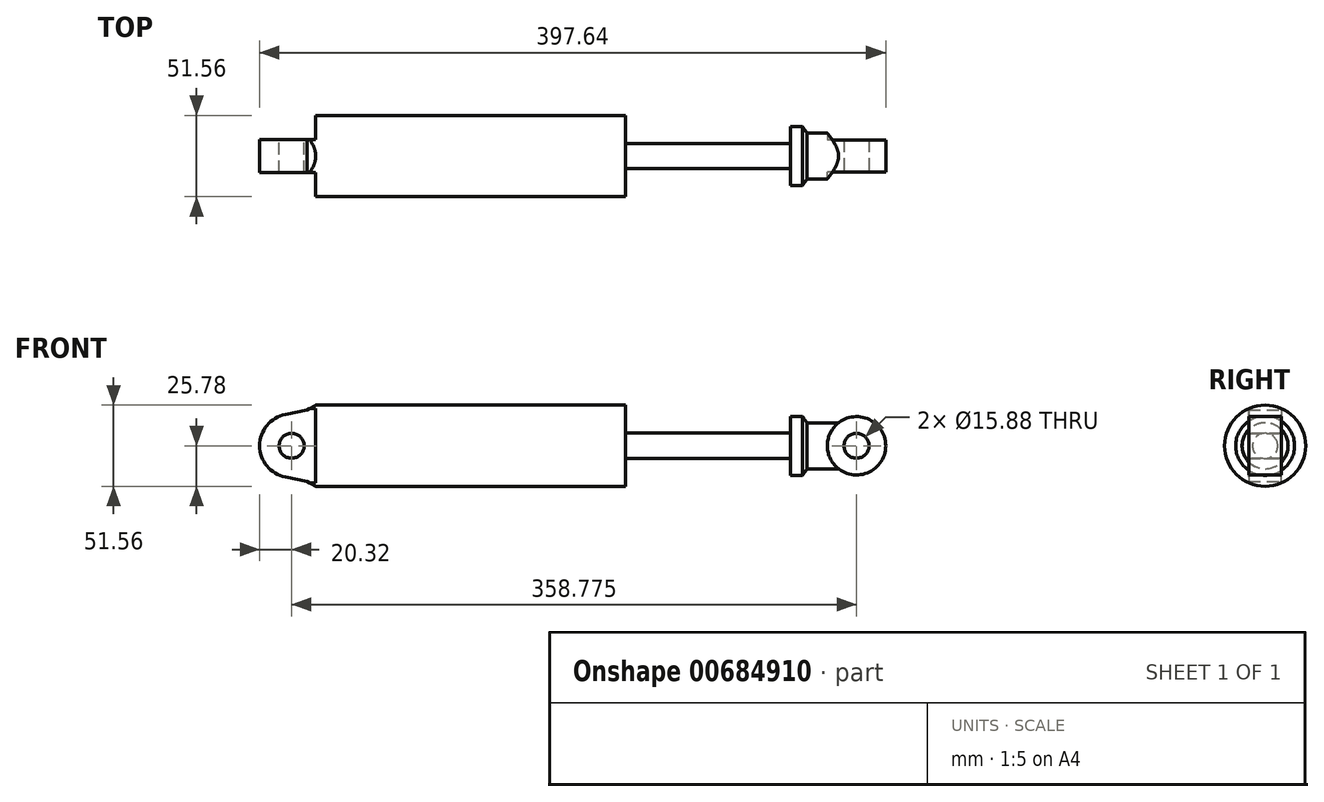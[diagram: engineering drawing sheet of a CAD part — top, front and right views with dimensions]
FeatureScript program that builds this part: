
annotation { "Feature Type Name" : "Feature", "Feature Type Description" : "" }
export const myFeature = defineFeature(function(context is Context, id is Id, definition is map)
    precondition{}
    {
        {
            var Q0;
            Q0=qCreatedBy(makeId("Front.planeOp"),FACE);
            var sketch = newSketch(context, id + "F0", { "sketchPlane" : qUnion([Q0])});
            skLineSegment(sketch, "E0", {"start": v(-164.73, 0) * mm, "end": v(453.96, 0) * mm, "construction": true});
            skLineSegment(sketch, "E1", {"start": v(0, 25.78) * mm, "end": v(232.41, 25.78) * mm});
            skLineSegment(sketch, "E2", {"start": v(232.41, 25.78) * mm, "end": v(232.41, 8) * mm});
            skLineSegment(sketch, "E3", {"start": v(232.41, 8) * mm, "end": v(337.19, 8) * mm});
            skLineSegment(sketch, "E4", {"start": v(337.19, 8) * mm, "end": v(337.19, 18.73) * mm});
            skLineSegment(sketch, "E5", {"start": v(337.19, 18.73) * mm, "end": v(344.8, 18.73) * mm});
            skLineSegment(sketch, "E6", {"start": v(344.8, 18.73) * mm, "end": v(347.6, 14.6) * mm});
            skLineSegment(sketch, "E7", {"start": v(347.6, 14.6) * mm, "end": v(409.83, 14.6) * mm});
            skLineSegment(sketch, "E8", {"start": v(0, 0) * mm, "end": v(409.83, 0) * mm});
            skLineSegment(sketch, "E9", {"start": v(409.83, 0) * mm, "end": v(409.83, 14.6) * mm});
            skLineSegment(sketch, "E10", {"start": v(0, 25.78) * mm, "end": v(0, 0) * mm});
            skSolve(sketch);
        }
        {
            var Q0;
            Q0 = qSketchRegion(id + "F0", true);
            var Q1;
            Q1=sQuery(id+"F0.wireOp",EDGE,"E0");
            revolve(context, id + "F1", {"surfaceOperationType" : NewSurfaceOperationType.NEW, "entities" : qUnion([Q0]), "axis" : qUnion([Q1]), "revolveType" : RevolveType.FULL});
        }
        {
            var Q0;
            Q0=makeQuery(id+"F1.opRevolve","SWEPT_FACE",FACE,{"disambiguationData":[OSD([sQuery(id+"F0.wireOp",EDGE,"E10")])]});
            var sketch = newSketch(context, id + "F2", { "sketchPlane" : qUnion([Q0])});
            skLineSegment(sketch, "E11", {"start": v(0, 48.27) * mm, "end": v(0, -54.75) * mm, "construction": true});
            skLineSegment(sketch, "E12", {"start": v(-46.95, 0) * mm, "end": v(40.07, 0) * mm, "construction": true});
            skLineSegment(sketch, "E13.bottom", {"start": v(48.51, 31.75) * mm, "end": v(10.41, 31.75) * mm});
            skLineSegment(sketch, "E13.top", {"start": v(48.51, -31.75) * mm, "end": v(10.41, -31.75) * mm});
            skLineSegment(sketch, "E13.left", {"start": v(48.51, 31.75) * mm, "end": v(48.51, -31.75) * mm});
            skLineSegment(sketch, "E13.right", {"start": v(10.41, 31.75) * mm, "end": v(10.41, -31.75) * mm});
            skPoint(sketch, "E13.middle", {"position": v(29.46, 0) * mm});
            skLineSegment(sketch, "E14.MirrorCS", {"start": v(-48.51, 31.75) * mm, "end": v(-48.51, -31.75) * mm});
            skLineSegment(sketch, "E15.MirrorCS", {"start": v(-48.51, 31.75) * mm, "end": v(-10.41, 31.75) * mm});
            skPoint(sketch, "E16.MirrorP", {"position": v(-29.46, 0) * mm});
            skLineSegment(sketch, "E17.MirrorCS", {"start": v(-48.51, -31.75) * mm, "end": v(-10.41, -31.75) * mm});
            skLineSegment(sketch, "E18.MirrorCS", {"start": v(-10.41, 31.75) * mm, "end": v(-10.41, -31.75) * mm});
            skSolve(sketch);
        }
        {
            var Q0;
            Q0 = qSketchRegion(id + "F2", true);
            extrude(context, id + "F3", {"entities" : qUnion([Q0]), "operationType" : NewBodyOperationType.REMOVE, "oppositeDirection" : true, "depth" : 35.56 * mm, "offsetDistance" : 25.4 * mm});
        }
        {
            var Q0;
            Q0=makeQuery(id+"F3.boolean.opBoolean","COPY",FACE,{"derivedFrom":makeQuery(id+"F3.opExtrude","SWEPT_FACE",FACE,{"disambiguationData":[OSD([sQuery(id+"F2.wireOp",EDGE,"E18.MirrorCS")])]})});
            var sketch = newSketch(context, id + "F4", { "sketchPlane" : qUnion([Q0])});
            skCircle(sketch, "E19", {"center": v(-20.32, 0) * mm, "radius": 20.32 * mm, "construction": true});
            skLineSegment(sketch, "E20", {"start": v(-35.56, 25.78) * mm, "end": v(-30.06, 22.6) * mm});
            skLineSegment(sketch, "E21", {"start": v(0, 0) * mm, "end": v(-64.15, 0) * mm, "construction": true});
            skLineSegment(sketch, "E22", {"start": v(-35.56, 25.78) * mm, "end": v(-35.56, -25.78) * mm, "construction": true});
            skLineSegment(sketch, "E23", {"start": v(-30.06, 22.6) * mm, "end": v(-16.43, 19.94) * mm});
            skLineSegment(sketch, "E24.MirrorCS", {"start": v(-30.06, -22.6) * mm, "end": v(-16.43, -19.94) * mm});
            skLineSegment(sketch, "E25.MirrorCS", {"start": v(-35.56, -25.78) * mm, "end": v(-30.06, -22.6) * mm});
            skArc(sketch, "E26", {"start": v(-16.43, 19.94) * mm, "mid": v(0, 0) * mm, "end": v(-16.43, -19.94) * mm});
            skCircle(sketch, "E27", {"center": v(-20.32, 0) * mm, "radius": 7.94 * mm});
            skLineSegment(sketch, "E28", {"start": v(-35.56, 25.78) * mm, "end": v(10.16, 25.78) * mm});
            skLineSegment(sketch, "E29.MirrorCS", {"start": v(-35.56, -25.78) * mm, "end": v(10.16, -25.78) * mm});
            skLineSegment(sketch, "E30", {"start": v(10.16, -25.78) * mm, "end": v(10.16, 25.78) * mm});
            skSolve(sketch);
        }
        {
            var Q0;
            Q0 = qSketchRegion(id + "F4", true);
            var Q1;
            Q1=makeQuery(id+"F3.boolean.opBoolean","COPY",FACE,{"derivedFrom":makeQuery(id+"F3.opExtrude","SWEPT_FACE",FACE,{"disambiguationData":[OSD([sQuery(id+"F2.wireOp",EDGE,"E13.right")])]})});
            extrude(context, id + "F5", {"entities" : qUnion([Q0]), "operationType" : NewBodyOperationType.REMOVE, "endBound" : BoundingType.UP_TO_SURFACE, "oppositeDirection" : true, "depth" : 25.4 * mm, "endBoundEntityFace" : qUnion([Q1]), "offsetDistance" : 25.4 * mm});
        }
        {
            var Q0;
            Q0=makeQuery(id+"F1.opRevolve","SWEPT_FACE",FACE,{"disambiguationData":[OSD([sQuery(id+"F0.wireOp",EDGE,"E9")])]});
            var sketch = newSketch(context, id + "F6", { "sketchPlane" : qUnion([Q0])});
            skLineSegment(sketch, "E31", {"start": v(-25.06, 0) * mm, "end": v(10.16, 0) * mm, "construction": true});
            skLineSegment(sketch, "E32", {"start": v(0, 36.45) * mm, "end": v(0, -31.45) * mm, "construction": true});
            skLineSegment(sketch, "E33.bottom", {"start": v(10.16, 12.7) * mm, "end": v(35.56, 12.7) * mm});
            skLineSegment(sketch, "E33.top", {"start": v(10.16, -12.7) * mm, "end": v(35.56, -12.7) * mm});
            skLineSegment(sketch, "E33.left", {"start": v(10.16, 12.7) * mm, "end": v(10.16, -12.7) * mm});
            skLineSegment(sketch, "E33.right", {"start": v(35.56, 12.7) * mm, "end": v(35.56, -12.7) * mm});
            skLineSegment(sketch, "E34.MirrorCS", {"start": v(-35.56, 12.7) * mm, "end": v(-35.56, -12.7) * mm});
            skLineSegment(sketch, "E35.MirrorCS", {"start": v(-10.16, 12.7) * mm, "end": v(-35.56, 12.7) * mm});
            skLineSegment(sketch, "E36.MirrorCS", {"start": v(-10.16, 12.7) * mm, "end": v(-10.16, -12.7) * mm});
            skLineSegment(sketch, "E37.MirrorCS", {"start": v(-10.16, -12.7) * mm, "end": v(-35.56, -12.7) * mm});
            skSolve(sketch);
        }
        {
            var Q0;
            Q0 = qSketchRegion(id + "F6", true);
            extrude(context, id + "F7", {"entities" : qUnion([Q0]), "operationType" : NewBodyOperationType.REMOVE, "oppositeDirection" : true, "depth" : 44.7 * mm, "offsetDistance" : 25.4 * mm});
        }
        {
            var Q0;
            Q0=makeQuery(id+"F7.boolean.opBoolean","COPY",FACE,{"derivedFrom":makeQuery(id+"F7.opExtrude","SWEPT_FACE",FACE,{"disambiguationData":[OSD([sQuery(id+"F6.wireOp",EDGE,"E33.left")])]})});
            var sketch = newSketch(context, id + "F8", { "sketchPlane" : qUnion([Q0])});
            skLineSegment(sketch, "E38", {"start": v(-418.1, 0) * mm, "end": v(-291.68, 0) * mm, "construction": true});
            skCircle(sketch, "E39", {"center": v(-20.32, 0) * mm, "radius": 7.74 * mm, "construction": true});
            skCircle(sketch, "E40", {"center": v(-379.1, 0) * mm, "radius": 18.54 * mm});
            skSolve(sketch);
        }
        {
            var Q0;
            Q0 = qSketchRegion(id + "F8", true);
            var Q1;
            Q1=makeQuery(id+"F7.boolean.opBoolean","COPY",FACE,{"derivedFrom":makeQuery(id+"F7.opExtrude","SWEPT_FACE",FACE,{"disambiguationData":[OSD([sQuery(id+"F6.wireOp",EDGE,"E36.MirrorCS")])]})});
            extrude(context, id + "F9", {"entities" : qUnion([Q0]), "operationType" : NewBodyOperationType.ADD, "endBound" : BoundingType.UP_TO_SURFACE, "oppositeDirection" : true, "depth" : 25.4 * mm, "endBoundEntityFace" : qUnion([Q1]), "offsetDistance" : 25.4 * mm});
        }
        {
            var Q0;
            Q0=qCreatedBy(makeId("Front.planeOp"),FACE);
            var sketch = newSketch(context, id + "F10", { "sketchPlane" : qUnion([Q0])});
            skLineSegment(sketch, "E41", {"start": v(-423.32, 0) * mm, "end": v(-348.96, 0) * mm, "construction": true});
            skLineSegment(sketch, "E42", {"start": v(418.77, 0) * mm, "end": v(354.73, 0) * mm, "construction": true});
            skCircle(sketch, "E43", {"center": v(379.1, 0) * mm, "radius": 6.7 * mm, "construction": true});
            skArc(sketch, "E44", {"start": v(390.52, 14.6) * mm, "mid": v(397.64, 0) * mm, "end": v(390.52, -14.6) * mm});
            skLineSegment(sketch, "E45", {"start": v(390.52, 14.6) * mm, "end": v(409.83, 14.6) * mm});
            skLineSegment(sketch, "E46", {"start": v(390.52, -14.6) * mm, "end": v(409.83, -14.6) * mm});
            skLineSegment(sketch, "E47", {"start": v(409.83, 14.6) * mm, "end": v(409.83, -14.6) * mm});
            skSolve(sketch);
        }
        {
            var Q0;
            Q0 = qSketchRegion(id + "F10", true);
            extrude(context, id + "F11", {"entities" : qUnion([Q0]), "operationType" : NewBodyOperationType.REMOVE, "depth" : 25.4 * mm, "offsetDistance" : 25.4 * mm, "symmetric" : true});
        }
        {
            var Q0;
            Q0=makeQuery(id+"F9.boolean.opBoolean","MERGE",FACE,{"derivedFrom":[makeQuery(id+"F7.boolean.opBoolean","COPY",FACE,{"derivedFrom":makeQuery(id+"F7.opExtrude","SWEPT_FACE",FACE,{"disambiguationData":[OSD([sQuery(id+"F6.wireOp",EDGE,"E33.left")])]})}),makeQuery(id+"F9.opExtrude","CAP_FACE",FACE,{"disambiguationData":[OSD([sQuery(id+"F8.wireOp",EDGE,"E40")])],"isStart":true})]});
            var sketch = newSketch(context, id + "F12", { "sketchPlane" : qUnion([Q0])});
            skArc(sketch, "E48", {"start": v(-365.55, 12.66) * mm, "mid": v(-360.55, 0) * mm, "end": v(-365.55, -12.66) * mm});
            skLineSegment(sketch, "E49", {"start": v(-365.55, 12.66) * mm, "end": v(-365.55, -12.66) * mm});
            skSolve(sketch);
        }
        {
            var Q0;
            Q0 = qSketchRegion(id + "F12", true);
            extrude(context, id + "F13", {"entities" : qUnion([Q0]), "operationType" : NewBodyOperationType.REMOVE, "depth" : 25.4 * mm, "offsetDistance" : 25.4 * mm});
        }
        {
            var Q0;
            {var subQ0=sQuery(id+"F6.wireOp",EDGE,"E36.MirrorCS");Q0=makeQuery(id+"F9.boolean.opBoolean","MERGE",FACE,{"derivedFrom":[makeQuery(id+"F7.boolean.opBoolean","COPY",FACE,{"derivedFrom":makeQuery(id+"F7.opExtrude","SWEPT_FACE",FACE,{"disambiguationData":[OSD([subQ0])]})}),makeQuery(id+"F9.opExtrude","CAP_FACE",FACE,{"disambiguationData":[OSD([subQ0])],"isStart":false})]});}
            var sketch = newSketch(context, id + "F14", { "sketchPlane" : qUnion([Q0])});
            skLineSegment(sketch, "E50", {"start": v(365.13, 12.2) * mm, "end": v(365.13, -12.2) * mm});
            skArc(sketch, "E51", {"start": v(365.13, 12.2) * mm, "mid": v(360.55, 0) * mm, "end": v(365.13, -12.2) * mm});
            skSolve(sketch);
        }
        {
            var Q0;
            Q0 = qSketchRegion(id + "F14", true);
            extrude(context, id + "F15", {"entities" : qUnion([Q0]), "operationType" : NewBodyOperationType.REMOVE, "depth" : 25.4 * mm, "offsetDistance" : 25.4 * mm});
        }
        {
            var Q0;
            {var subQ0=sQuery(id+"F6.wireOp",EDGE,"E36.MirrorCS");Q0=makeQuery(id+"F15.boolean.opBoolean","MERGE",FACE,{"derivedFrom":[makeQuery(id+"F9.boolean.opBoolean","MERGE",FACE,{"derivedFrom":[makeQuery(id+"F7.boolean.opBoolean","COPY",FACE,{"derivedFrom":makeQuery(id+"F7.opExtrude","SWEPT_FACE",FACE,{"disambiguationData":[OSD([subQ0])]})}),makeQuery(id+"F9.opExtrude","CAP_FACE",FACE,{"disambiguationData":[OSD([subQ0])],"isStart":false})]}),makeQuery(id+"F15.opExtrude","CAP_FACE",FACE,{"disambiguationData":[OSD([sQuery(id+"F14.wireOp",EDGE,"E50"),sQuery(id+"F14.wireOp",EDGE,"E51")])],"isStart":true})]});}
            var sketch = newSketch(context, id + "F16", { "sketchPlane" : qUnion([Q0])});
            skCircle(sketch, "E52", {"center": v(379.1, 0) * mm, "radius": 7.94 * mm});
            skSolve(sketch);
        }
        {
            var Q0;
            Q0 = qSketchRegion(id + "F16", true);
            extrude(context, id + "F17", {"entities" : qUnion([Q0]), "operationType" : NewBodyOperationType.REMOVE, "endBound" : BoundingType.THROUGH_ALL, "oppositeDirection" : true, "depth" : 25.4 * mm, "offsetDistance" : 25.4 * mm});
        }
    });
